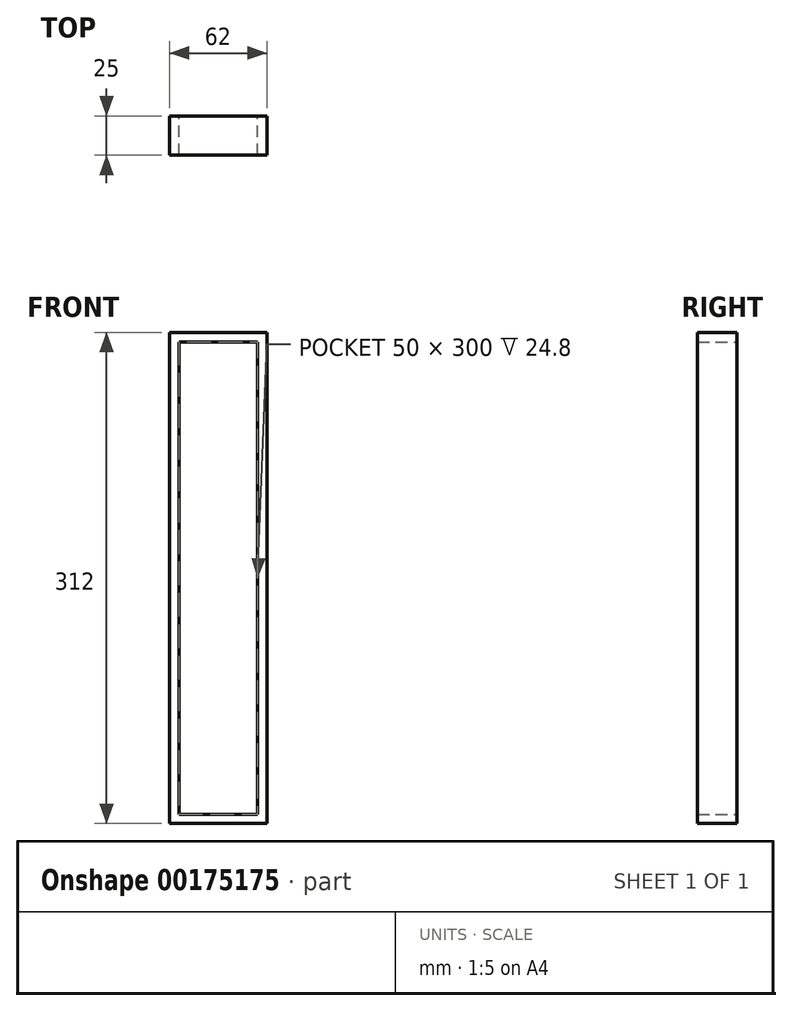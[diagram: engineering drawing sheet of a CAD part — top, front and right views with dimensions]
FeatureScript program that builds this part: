
annotation { "Feature Type Name" : "Feature", "Feature Type Description" : "" }
export const myFeature = defineFeature(function(context is Context, id is Id, definition is map)
    precondition{}
    {
        {
            var Q0;
            Q0=qCreatedBy(makeId("Front.planeOp"),FACE);
            var sketch = newSketch(context, id + "F0", { "sketchPlane" : qUnion([Q0])});
            skLineSegment(sketch, "E0.bottom", {"start": v(25, 150) * mm, "end": v(-25, 150) * mm});
            skLineSegment(sketch, "E0.top", {"start": v(25, -150) * mm, "end": v(-25, -150) * mm});
            skLineSegment(sketch, "E0.left", {"start": v(25, 150) * mm, "end": v(25, -150) * mm});
            skLineSegment(sketch, "E0.right", {"start": v(-25, 150) * mm, "end": v(-25, -150) * mm});
            skPoint(sketch, "E0.middle", {"position": v(0, 0) * mm});
            skLineSegment(sketch, "E1.bottom", {"start": v(31, 156) * mm, "end": v(-31, 156) * mm});
            skLineSegment(sketch, "E1.top", {"start": v(31, -156) * mm, "end": v(-31, -156) * mm});
            skLineSegment(sketch, "E1.left", {"start": v(31, 156) * mm, "end": v(31, -156) * mm});
            skLineSegment(sketch, "E1.right", {"start": v(-31, 156) * mm, "end": v(-31, -156) * mm});
            skSolve(sketch);
        }
        {
            var Q0;
            Q0 = qSketchRegion(id + "F0", true);
            var Q1;
            Q1=makeQuery(id+"F0.imprint","IMPRINT",FACE,{"disambiguationData":[TD([[makeQuery(id+"F0.imprint","IMPRINT",EDGE,{"derivedFrom":sQuery(id+"F0.wireOp",EDGE,"E0.bottom")}),1.0]])]});
            extrude(context, id + "F1", {"entities" : qUnion([Q0, Q1]), "depth" : .2 * mm});
        }
        {
            var Q0;
            Q0=makeQuery(id+"F0.imprint","IMPRINT",FACE,{"disambiguationData":[TD([[makeQuery(id+"F0.imprint","IMPRINT",EDGE,{"derivedFrom":sQuery(id+"F0.wireOp",EDGE,"E0.bottom")}),-1.0]])]});
            extrude(context, id + "F2", {"entities" : qUnion([Q0]), "operationType" : NewBodyOperationType.ADD, "depth" : 25 * mm});
        }
    });
